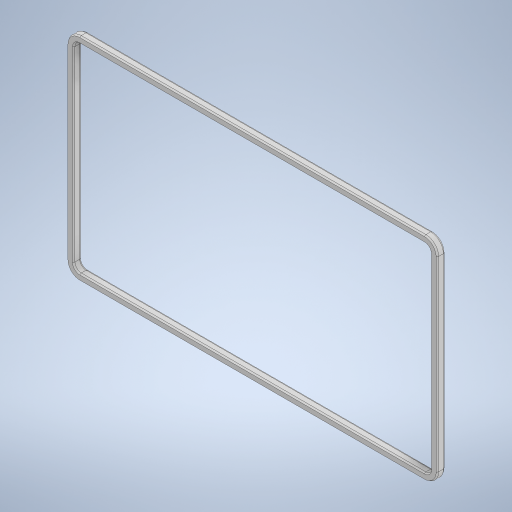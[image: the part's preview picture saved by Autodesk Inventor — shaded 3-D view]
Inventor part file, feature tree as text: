
AUTODESK INVENTOR PART (.ipt)
format: ipt  version: 2023 (Build 270158000, 158)  size: 308,224 bytes
history: native  units: in
note: dims shown in document units (in); Inventor stores cm internally (conversion verified against a paired STEP export)
features: chamfer x4, fillet x2, extrude x1, sketch x1
ambient origin geometry x8: Origin, YZ Plane, XZ Plane, XY Plane, X Axis, Y Axis, Z Axis, Center Point
bodies: Solid1 (feature_tree)
feature tree (8):
  extrude  "Extrusion1"  Depth=2.6378in
  fillet  "Fillet1"  Radius=0.0787in
  fillet  "Fillet2"  Radius=0.0984in
  chamfer  "Chamfer1"  Distance=0.0787in
  chamfer  "Chamfer2"  Distance=0.1575in
  chamfer  "Chamfer3"  Distance=0.0787in Angle=30.0deg
  chamfer  "Chamfer4"  Distance=0.0787in Angle=30.0deg
  sketch  "Sketch1"  dims[d0=4.6063in d1=2.6378in d2=0.0787in d3=0.0984in d4=0.0in d5=0.0787in d6=0.1575in d11=0.0197in d12=0.0787in d13=30.0deg d14=0.0197in d15=0.0787in d16=30.0deg d17=0.0197in d18=0.0787in d19=30.0deg d20=0.0197in d21=0.0787in d22=30.0deg]
